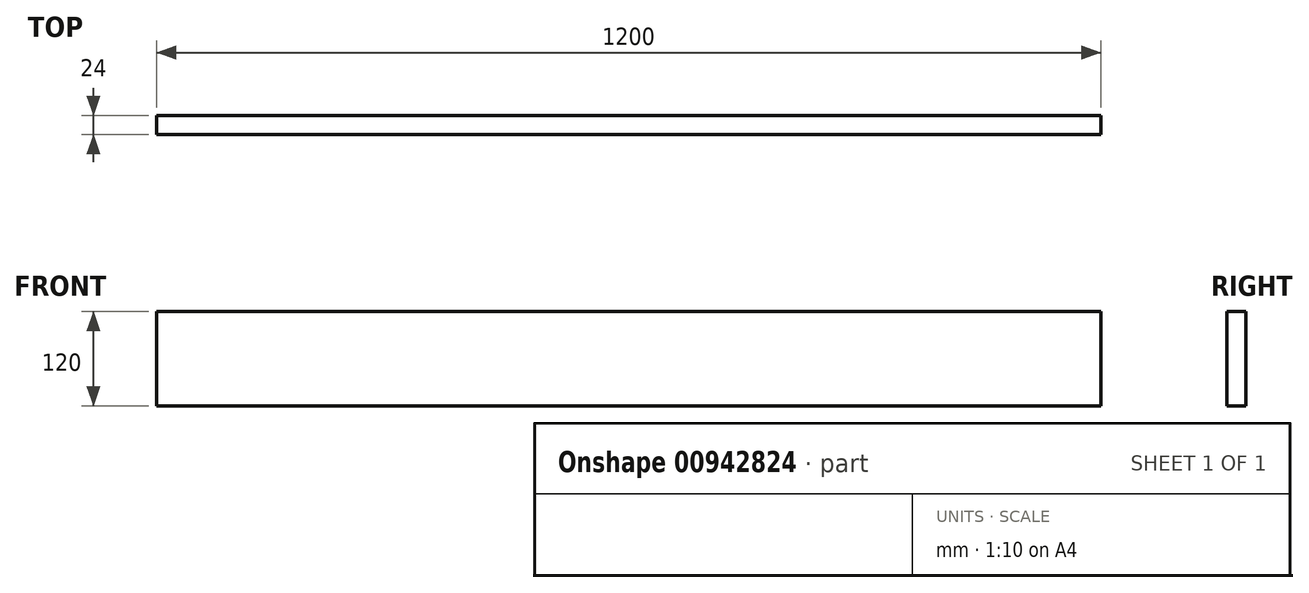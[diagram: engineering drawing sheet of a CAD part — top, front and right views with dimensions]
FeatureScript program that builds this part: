
annotation { "Feature Type Name" : "Feature", "Feature Type Description" : "" }
export const myFeature = defineFeature(function(context is Context, id is Id, definition is map)
    precondition{}
    {
        {
            var Q0;
            Q0=qCreatedBy(makeId("Front.planeOp"),FACE);
            var sketch = newSketch(context, id + "F0", { "sketchPlane" : qUnion([Q0])});
            skLineSegment(sketch, "E0.bottom", {"start": v(-603.18, -95.76) * mm, "end": v(596.82, -95.76) * mm});
            skLineSegment(sketch, "E0.top", {"start": v(-603.18, -215.76) * mm, "end": v(596.82, -215.76) * mm});
            skLineSegment(sketch, "E0.left", {"start": v(-603.18, -95.76) * mm, "end": v(-603.18, -215.76) * mm});
            skLineSegment(sketch, "E0.right", {"start": v(596.82, -95.76) * mm, "end": v(596.82, -215.76) * mm});
            skSolve(sketch);
        }
        {
            var Q0;
            Q0=makeQuery(id+"F0.imprint","IMPRINT",FACE,{"disambiguationData":[TD([[makeQuery(id+"F0.imprint","IMPRINT",EDGE,{"derivedFrom":sQuery(id+"F0.wireOp",EDGE,"E0.bottom")}),-1.0]])]});
            extrude(context, id + "F1", {"entities" : qUnion([Q0]), "depth" : 24 * mm, "offsetDistance" : 25 * mm});
        }
    });
